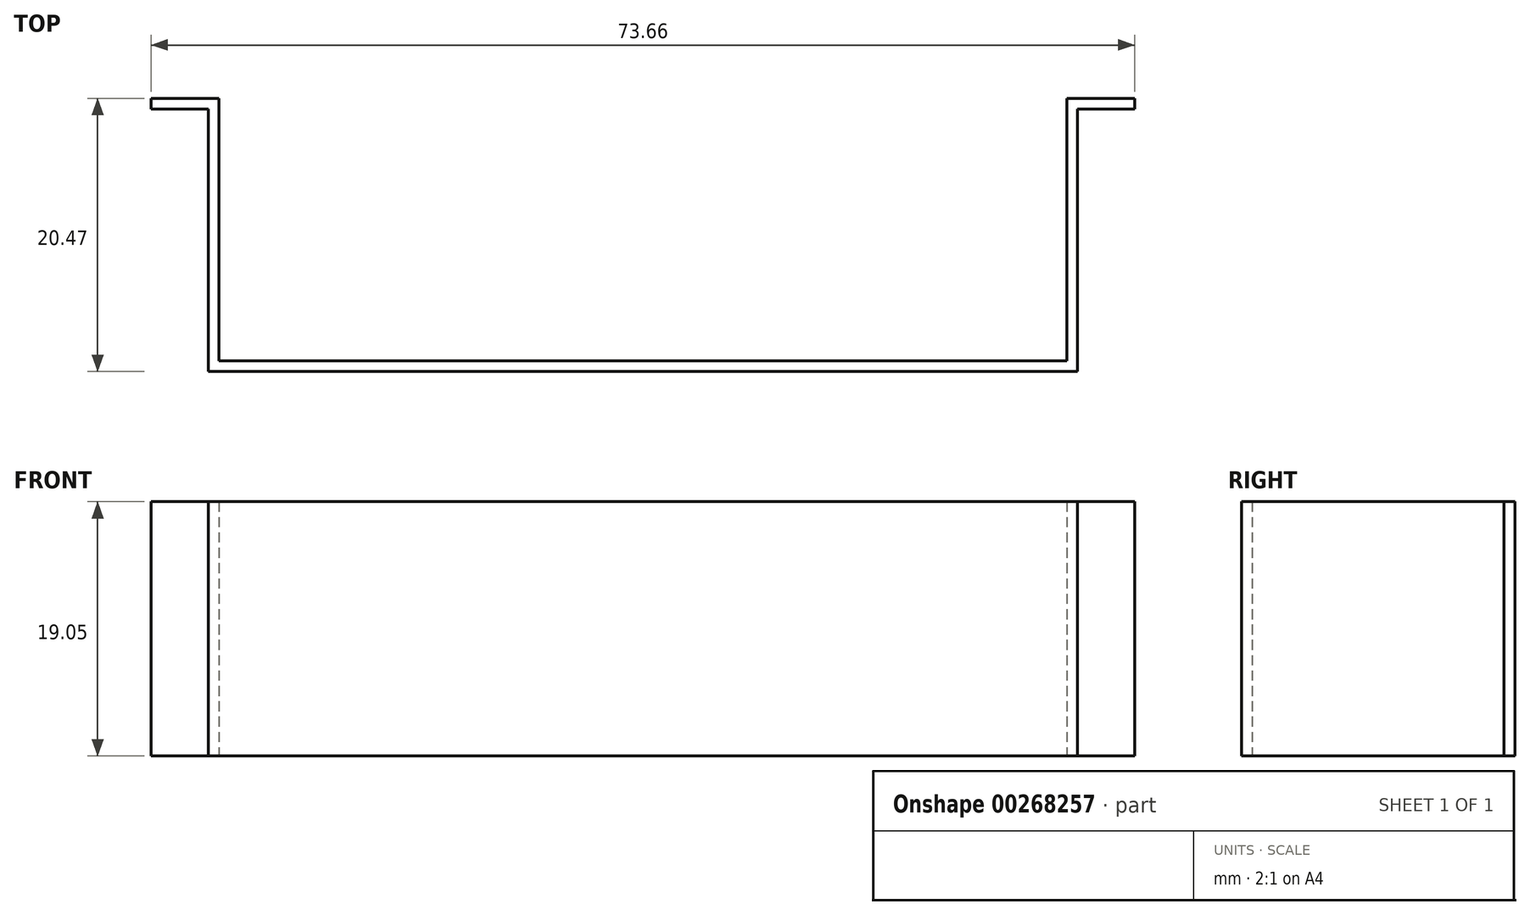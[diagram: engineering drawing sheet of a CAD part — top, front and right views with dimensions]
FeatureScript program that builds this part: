
annotation { "Feature Type Name" : "Feature", "Feature Type Description" : "" }
export const myFeature = defineFeature(function(context is Context, id is Id, definition is map)
    precondition{}
    {
        {
            var Q0;
            Q0=qCreatedBy(makeId("Top.planeOp"),FACE);
            var sketch = newSketch(context, id + "F0", { "sketchPlane" : qUnion([Q0])});
            skLineSegment(sketch, "E0", {"start": v(0, -19.67) * mm, "end": v(31.75, -19.67) * mm});
            skLineSegment(sketch, "E1", {"start": v(31.75, -19.67) * mm, "end": v(31.75, 0) * mm});
            skLineSegment(sketch, "E2", {"start": v(31.75, 0) * mm, "end": v(36.83, 0) * mm});
            skLineSegment(sketch, "E3.0", {"start": v(32.55, -0.8) * mm, "end": v(36.83, -0.8) * mm});
            skLineSegment(sketch, "E3.1", {"start": v(32.55, -20.47) * mm, "end": v(32.55, -0.8) * mm});
            skLineSegment(sketch, "E3.2", {"start": v(0, -20.47) * mm, "end": v(32.55, -20.47) * mm});
            skLineSegment(sketch, "E4", {"start": v(36.83, 0) * mm, "end": v(36.83, -0.8) * mm});
            skLineSegment(sketch, "E5.MirrorCS", {"start": v(-32.55, -20.47) * mm, "end": v(-32.55, -0.8) * mm});
            skLineSegment(sketch, "E6.MirrorCS", {"start": v(-31.75, -19.67) * mm, "end": v(-31.75, 0) * mm});
            skLineSegment(sketch, "E7.MirrorCS", {"start": v(-31.75, 0) * mm, "end": v(-36.83, 0) * mm});
            skLineSegment(sketch, "E8.MirrorCS", {"start": v(-32.55, -0.8) * mm, "end": v(-36.83, -0.8) * mm});
            skLineSegment(sketch, "E9.MirrorCS", {"start": v(0, -20.47) * mm, "end": v(-32.55, -20.47) * mm});
            skLineSegment(sketch, "E10.MirrorCS", {"start": v(0, -19.67) * mm, "end": v(-31.75, -19.67) * mm});
            skLineSegment(sketch, "E11.MirrorCS", {"start": v(-36.83, 0) * mm, "end": v(-36.83, -0.8) * mm});
            skSolve(sketch);
        }
        {
            var Q0;
            Q0=makeQuery(id+"F0.imprint","IMPRINT",FACE,{"disambiguationData":[TD([[makeQuery(id+"F0.imprint","IMPRINT",EDGE,{"derivedFrom":sQuery(id+"F0.wireOp",EDGE,"E0")}),-1.0]])]});
            extrude(context, id + "F1", {"entities" : qUnion([Q0]), "depth" : 19.05 * mm});
        }
    });
